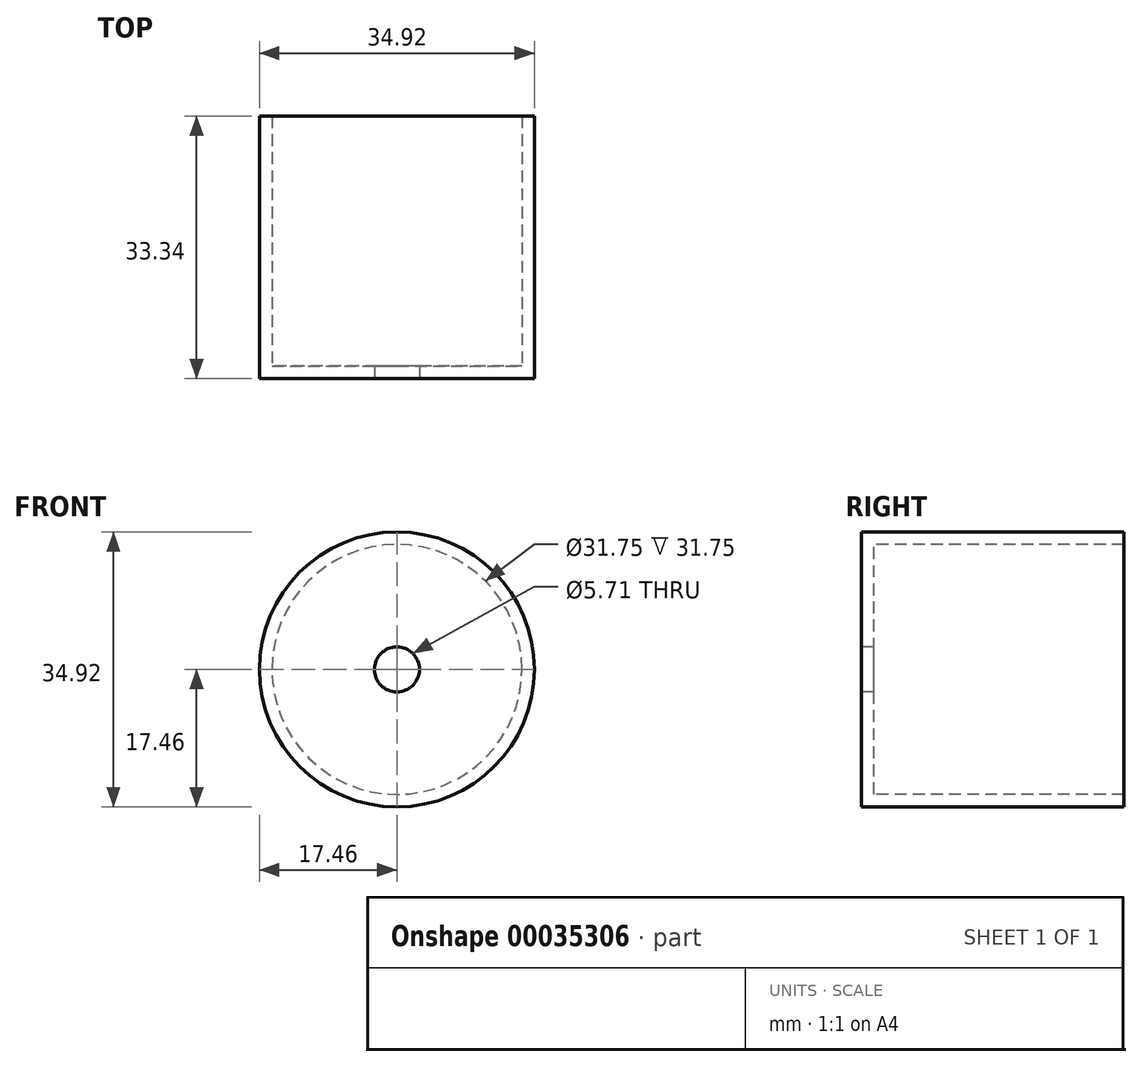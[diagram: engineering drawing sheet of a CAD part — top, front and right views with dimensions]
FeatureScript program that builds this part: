
annotation { "Feature Type Name" : "Feature", "Feature Type Description" : "" }
export const myFeature = defineFeature(function(context is Context, id is Id, definition is map)
    precondition{}
    {
        {
            var Q0;
            Q0=qCreatedBy(makeId("Right.planeOp"),FACE);
            var sketch = newSketch(context, id + "F0", { "sketchPlane" : qUnion([Q0])});
            skLineSegment(sketch, "E0.bottom", {"start": v(-16.67, 17.46) * mm, "end": v(16.67, 17.46) * mm});
            skLineSegment(sketch, "E0.right", {"start": v(16.67, 17.46) * mm, "end": v(16.67, 15.88) * mm});
            skLineSegment(sketch, "E1", {"start": v(-16.62, 0) * mm, "end": v(15.21, 0) * mm, "construction": true});
            skLineSegment(sketch, "E2", {"start": v(-16.67, 2.86) * mm, "end": v(-15.08, 2.86) * mm});
            skLineSegment(sketch, "E3", {"start": v(-15.08, 2.86) * mm, "end": v(-15.08, 15.88) * mm});
            skLineSegment(sketch, "E4", {"start": v(-15.08, 15.87) * mm, "end": v(16.67, 15.87) * mm});
            skLineSegment(sketch, "E5", {"start": v(-16.67, 17.46) * mm, "end": v(-16.67, 2.86) * mm});
            skSolve(sketch);
        }
        {
            var Q0;
            Q0=makeQuery(id+"F0.imprint","IMPRINT",FACE,{"disambiguationData":[TD([[makeQuery(id+"F0.imprint","IMPRINT",EDGE,{"derivedFrom":sQuery(id+"F0.wireOp",EDGE,"E0.bottom")}),-1.0]])]});
            var Q1;
            Q1=sQuery(id+"F0.wireOp",EDGE,"E1");
            revolve(context, id + "F1", {"entities" : qUnion([Q0]), "axis" : qUnion([Q1]), "revolveType" : RevolveType.FULL});
        }
    });
